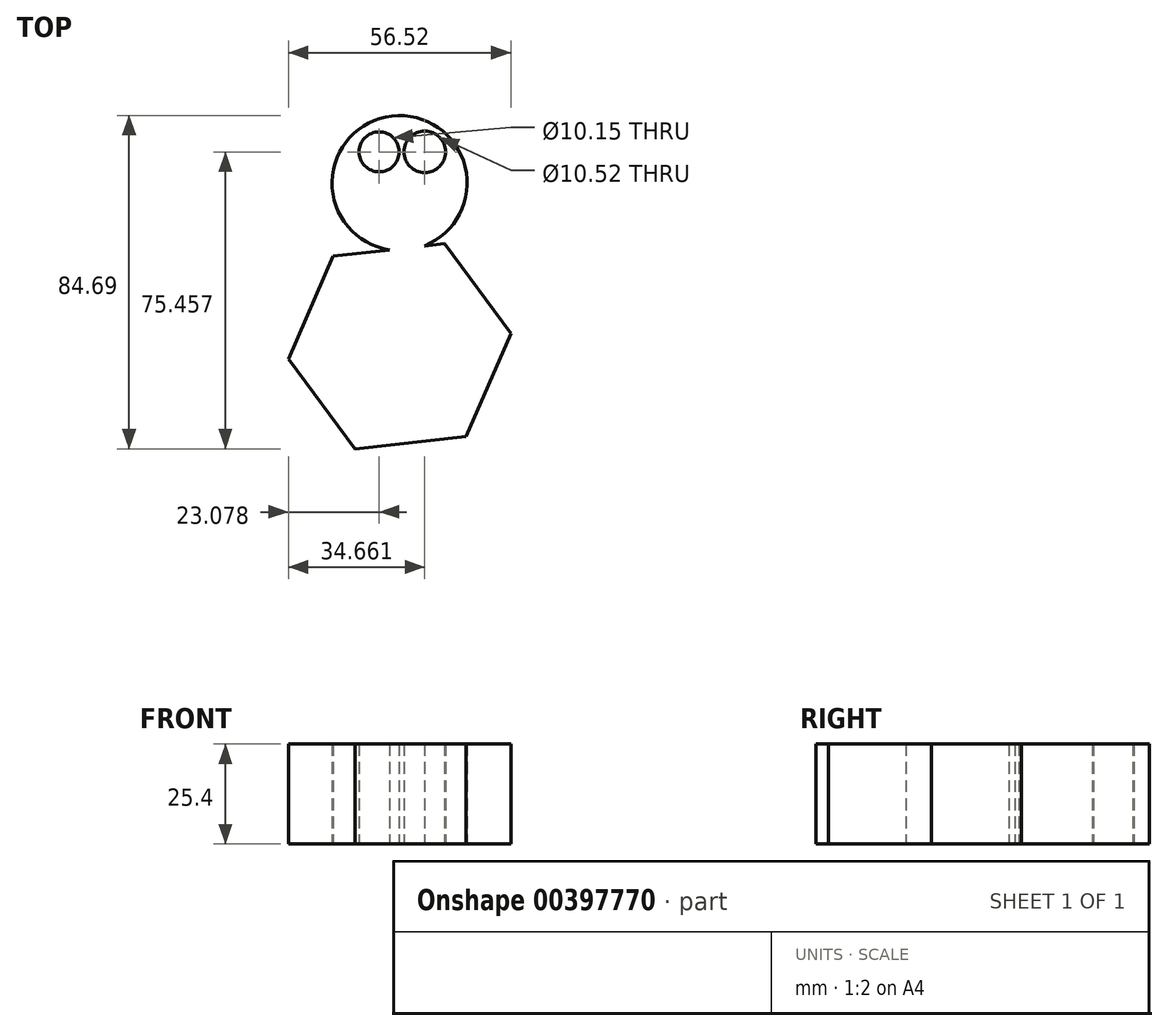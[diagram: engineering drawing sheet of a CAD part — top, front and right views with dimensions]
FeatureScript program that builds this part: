
annotation { "Feature Type Name" : "Feature", "Feature Type Description" : "" }
export const myFeature = defineFeature(function(context is Context, id is Id, definition is map)
    precondition{}
    {
        {
            var Q0;
            Q0=qCreatedBy(makeId("Top.planeOp"),FACE);
            var sketch = newSketch(context, id + "F0", { "sketchPlane" : qUnion([Q0])});
            skCircle(sketch, "E0", {"center": v(0, 24.23) * mm, "radius": 17.16 * mm});
            skCircle(sketch, "E1", {"center": v(6.4, 32.16) * mm, "radius": 5.26 * mm});
            skLineSegment(sketch, "E2", {"start": v(0, 17.22) * mm, "end": v(-7.92, 17.22) * mm});
            skLineSegment(sketch, "E3", {"start": v(0, 17.22) * mm, "end": v(8.53, 17.22) * mm});
            skCircle(sketch, "E4.cCircle", {"center": v(0, -17.23) * mm, "radius": 24.63 * mm, "construction": true});
            skLineSegment(sketch, "E4.0", {"start": v(-11.36, -43.3) * mm, "end": v(-28.26, -20.42) * mm});
            skLineSegment(sketch, "E4.1", {"start": v(-28.26, -20.42) * mm, "end": v(-16.9, 5.65) * mm});
            skLineSegment(sketch, "E4.2", {"start": v(-16.9, 5.65) * mm, "end": v(11.36, 8.84) * mm});
            skLineSegment(sketch, "E4.3", {"start": v(11.36, 8.84) * mm, "end": v(28.26, -14.03) * mm});
            skLineSegment(sketch, "E4.4", {"start": v(28.26, -14.03) * mm, "end": v(16.9, -40.1) * mm});
            skLineSegment(sketch, "E4.5", {"start": v(16.9, -40.1) * mm, "end": v(-11.36, -43.3) * mm});
            skPoint(sketch, "E4.0.midPoint", {"position": v(-19.81, -31.86) * mm});
            skPoint(sketch, "E5.center.orphan", {"position": v(-5.18, 32.16) * mm});
            skCircle(sketch, "E6", {"center": v(-5.18, 32.16) * mm, "radius": 5.07 * mm});
            skSolve(sketch);
        }
        {
            var Q0;
            Q0 = qSketchRegion(id + "F0", true);
            extrude(context, id + "F1", {"entities" : qUnion([Q0]), "depth" : 25.4 * mm});
        }
    });
